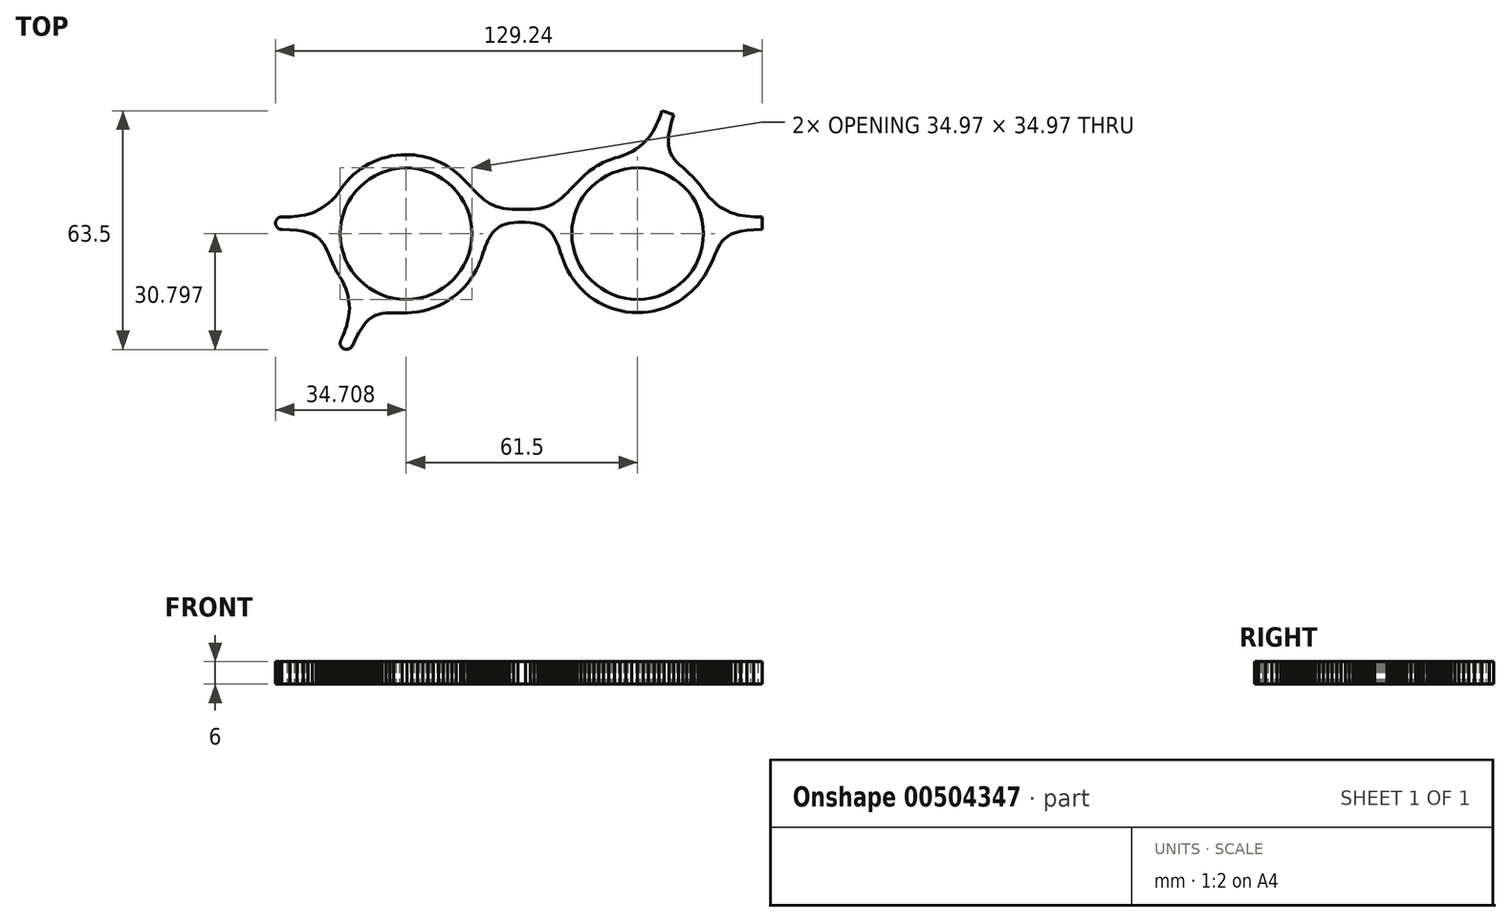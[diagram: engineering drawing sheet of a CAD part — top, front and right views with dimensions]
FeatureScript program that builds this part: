
annotation { "Feature Type Name" : "Feature", "Feature Type Description" : "" }
export const myFeature = defineFeature(function(context is Context, id is Id, definition is map)
    precondition{}
    {
        {
            var Q0;
            Q0=qCreatedBy(makeId("Top.planeOp"),FACE);
            var sketch = newSketch(context, id + "F0", { "sketchPlane" : qUnion([Q0])});
            skLineSegment(sketch, "E0", {"start": v(-47.15, 11.05) * mm, "end": v(-47.14, 11.06) * mm});
            skLineSegment(sketch, "E1", {"start": v(-47.14, 11.06) * mm, "end": v(-47.14, 11.06) * mm});
            skLineSegment(sketch, "E2", {"start": v(-47.14, 11.06) * mm, "end": v(-47.15, 11.05) * mm});
            skLineSegment(sketch, "E3", {"start": v(-47.15, 11.05) * mm, "end": v(-47.15, 11.05) * mm});
            skLineSegment(sketch, "E4", {"start": v(-47.15, 11.05) * mm, "end": v(-47.15, 11.04) * mm});
            skLineSegment(sketch, "E5", {"start": v(-47.15, 11.04) * mm, "end": v(-47.16, 11.04) * mm});
            skLineSegment(sketch, "E6", {"start": v(-47.16, 11.04) * mm, "end": v(-47.16, 11.04) * mm});
            skLineSegment(sketch, "E7", {"start": v(-47.16, 11.04) * mm, "end": v(-47.16, 11.03) * mm});
            skLineSegment(sketch, "E8", {"start": v(-47.16, 11.03) * mm, "end": v(-47.16, 11.03) * mm});
            skLineSegment(sketch, "E9", {"start": v(-47.16, 11.03) * mm, "end": v(-47.15, 11.04) * mm});
            skLineSegment(sketch, "E10", {"start": v(-47.15, 11.04) * mm, "end": v(-47.15, 11.05) * mm});
            skLineSegment(sketch, "E11", {"start": v(48.83, 11.04) * mm, "end": v(48.83, 11.04) * mm});
            skLineSegment(sketch, "E12", {"start": v(48.83, 11.04) * mm, "end": v(48.83, 11.05) * mm});
            skLineSegment(sketch, "E13", {"start": v(48.83, 11.05) * mm, "end": v(48.82, 11.05) * mm});
            skLineSegment(sketch, "E14", {"start": v(48.82, 11.05) * mm, "end": v(48.82, 11.05) * mm});
            skLineSegment(sketch, "E15", {"start": v(48.82, 11.05) * mm, "end": v(48.82, 11.06) * mm});
            skLineSegment(sketch, "E16", {"start": v(48.82, 11.06) * mm, "end": v(48.82, 11.06) * mm});
            skLineSegment(sketch, "E17", {"start": v(48.82, 11.06) * mm, "end": v(48.81, 11.06) * mm});
            skLineSegment(sketch, "E18", {"start": v(48.81, 11.06) * mm, "end": v(48.82, 11.06) * mm});
            skLineSegment(sketch, "E19", {"start": v(48.82, 11.06) * mm, "end": v(48.82, 11.05) * mm});
            skLineSegment(sketch, "E20", {"start": v(48.82, 11.05) * mm, "end": v(48.83, 11.04) * mm});
            skLineSegment(sketch, "E21", {"start": v(48.83, 11.04) * mm, "end": v(48.83, 11.03) * mm});
            skLineSegment(sketch, "E22", {"start": v(48.83, 11.03) * mm, "end": v(48.83, 11.03) * mm});
            skLineSegment(sketch, "E23", {"start": v(48.83, 11.03) * mm, "end": v(48.83, 11.04) * mm});
            skLineSegment(sketch, "E24", {"start": v(63.55, 3.53) * mm, "end": v(62.5, 3.56) * mm});
            skLineSegment(sketch, "E25", {"start": v(62.5, 3.56) * mm, "end": v(61.45, 3.62) * mm});
            skLineSegment(sketch, "E26", {"start": v(61.45, 3.62) * mm, "end": v(60.41, 3.72) * mm});
            skLineSegment(sketch, "E27", {"start": v(60.41, 3.72) * mm, "end": v(59.38, 3.86) * mm});
            skLineSegment(sketch, "E28", {"start": v(59.38, 3.86) * mm, "end": v(58.36, 4.07) * mm});
            skLineSegment(sketch, "E29", {"start": v(58.36, 4.07) * mm, "end": v(57.35, 4.33) * mm});
            skLineSegment(sketch, "E30", {"start": v(57.35, 4.33) * mm, "end": v(56.35, 4.67) * mm});
            skLineSegment(sketch, "E31", {"start": v(56.35, 4.67) * mm, "end": v(55.36, 5.1) * mm});
            skLineSegment(sketch, "E32", {"start": v(55.36, 5.1) * mm, "end": v(54.38, 5.6) * mm});
            skLineSegment(sketch, "E33", {"start": v(54.38, 5.6) * mm, "end": v(53.42, 6.21) * mm});
            skLineSegment(sketch, "E34", {"start": v(53.42, 6.21) * mm, "end": v(52.47, 6.93) * mm});
            skLineSegment(sketch, "E35", {"start": v(52.47, 6.93) * mm, "end": v(51.54, 7.76) * mm});
            skLineSegment(sketch, "E36", {"start": v(51.54, 7.76) * mm, "end": v(50.62, 8.72) * mm});
            skLineSegment(sketch, "E37", {"start": v(50.62, 8.72) * mm, "end": v(49.72, 9.8) * mm});
            skLineSegment(sketch, "E38", {"start": v(49.72, 9.8) * mm, "end": v(48.83, 11.03) * mm});
            skLineSegment(sketch, "E39", {"start": v(48.83, 11.03) * mm, "end": v(48.73, 11.17) * mm});
            skLineSegment(sketch, "E40", {"start": v(48.73, 11.17) * mm, "end": v(48.63, 11.31) * mm});
            skLineSegment(sketch, "E41", {"start": v(48.63, 11.31) * mm, "end": v(48.53, 11.45) * mm});
            skLineSegment(sketch, "E42", {"start": v(48.53, 11.45) * mm, "end": v(48.43, 11.59) * mm});
            skLineSegment(sketch, "E43", {"start": v(48.43, 11.59) * mm, "end": v(48.33, 11.72) * mm});
            skLineSegment(sketch, "E44", {"start": v(48.33, 11.72) * mm, "end": v(48.23, 11.86) * mm});
            skLineSegment(sketch, "E45", {"start": v(48.23, 11.86) * mm, "end": v(48.12, 12) * mm});
            skLineSegment(sketch, "E46", {"start": v(48.12, 12) * mm, "end": v(48.02, 12.13) * mm});
            skLineSegment(sketch, "E47", {"start": v(48.02, 12.13) * mm, "end": v(47.9, 12.26) * mm});
            skLineSegment(sketch, "E48", {"start": v(47.9, 12.26) * mm, "end": v(47.8, 12.4) * mm});
            skLineSegment(sketch, "E49", {"start": v(47.8, 12.4) * mm, "end": v(47.7, 12.52) * mm});
            skLineSegment(sketch, "E50", {"start": v(47.7, 12.52) * mm, "end": v(47.58, 12.65) * mm});
            skLineSegment(sketch, "E51", {"start": v(47.58, 12.65) * mm, "end": v(47.47, 12.78) * mm});
            skLineSegment(sketch, "E52", {"start": v(47.47, 12.78) * mm, "end": v(47.36, 12.91) * mm});
            skLineSegment(sketch, "E53", {"start": v(47.36, 12.91) * mm, "end": v(47.24, 13.04) * mm});
            skLineSegment(sketch, "E54", {"start": v(47.24, 13.04) * mm, "end": v(47.13, 13.16) * mm});
            skLineSegment(sketch, "E55", {"start": v(47.13, 13.16) * mm, "end": v(47.13, 13.16) * mm});
            skLineSegment(sketch, "E56", {"start": v(47.13, 13.16) * mm, "end": v(47.14, 13.16) * mm});
            skLineSegment(sketch, "E57", {"start": v(47.14, 13.16) * mm, "end": v(47.14, 13.16) * mm});
            skLineSegment(sketch, "E58", {"start": v(47.14, 13.16) * mm, "end": v(47.15, 13.16) * mm});
            skLineSegment(sketch, "E59", {"start": v(47.15, 13.16) * mm, "end": v(47.15, 13.16) * mm});
            skLineSegment(sketch, "E60", {"start": v(47.15, 13.16) * mm, "end": v(46.21, 14.17) * mm});
            skLineSegment(sketch, "E61", {"start": v(46.21, 14.17) * mm, "end": v(45.29, 15.08) * mm});
            skLineSegment(sketch, "E62", {"start": v(45.29, 15.08) * mm, "end": v(44.4, 15.9) * mm});
            skLineSegment(sketch, "E63", {"start": v(44.4, 15.9) * mm, "end": v(43.54, 16.66) * mm});
            skLineSegment(sketch, "E64", {"start": v(43.54, 16.66) * mm, "end": v(42.74, 17.39) * mm});
            skLineSegment(sketch, "E65", {"start": v(42.74, 17.39) * mm, "end": v(42, 18.11) * mm});
            skLineSegment(sketch, "E66", {"start": v(42, 18.11) * mm, "end": v(41.35, 18.85) * mm});
            skLineSegment(sketch, "E67", {"start": v(41.35, 18.85) * mm, "end": v(40.78, 19.64) * mm});
            skLineSegment(sketch, "E68", {"start": v(40.78, 19.64) * mm, "end": v(40.33, 20.5) * mm});
            skLineSegment(sketch, "E69", {"start": v(40.33, 20.5) * mm, "end": v(40, 21.44) * mm});
            skLineSegment(sketch, "E70", {"start": v(40, 21.44) * mm, "end": v(39.8, 22.52) * mm});
            skLineSegment(sketch, "E71", {"start": v(39.8, 22.52) * mm, "end": v(39.73, 23.75) * mm});
            skLineSegment(sketch, "E72", {"start": v(39.73, 23.75) * mm, "end": v(39.83, 25.15) * mm});
            skLineSegment(sketch, "E73", {"start": v(39.83, 25.15) * mm, "end": v(40.1, 26.75) * mm});
            skLineSegment(sketch, "E74", {"start": v(40.1, 26.75) * mm, "end": v(40.56, 28.58) * mm});
            skLineSegment(sketch, "E75", {"start": v(40.56, 28.58) * mm, "end": v(41.22, 30.66) * mm});
            skLineSegment(sketch, "E76", {"start": v(41.22, 30.66) * mm, "end": v(40.87, 30.78) * mm});
            skLineSegment(sketch, "E77", {"start": v(40.87, 30.78) * mm, "end": v(40.57, 30.88) * mm});
            skLineSegment(sketch, "E78", {"start": v(40.57, 30.88) * mm, "end": v(40.33, 30.96) * mm});
            skLineSegment(sketch, "E79", {"start": v(40.33, 30.96) * mm, "end": v(40.13, 31.03) * mm});
            skLineSegment(sketch, "E80", {"start": v(40.13, 31.03) * mm, "end": v(39.97, 31.09) * mm});
            skLineSegment(sketch, "E81", {"start": v(39.97, 31.09) * mm, "end": v(39.83, 31.13) * mm});
            skLineSegment(sketch, "E82", {"start": v(39.83, 31.13) * mm, "end": v(39.71, 31.17) * mm});
            skLineSegment(sketch, "E83", {"start": v(39.71, 31.17) * mm, "end": v(39.6, 31.21) * mm});
            skLineSegment(sketch, "E84", {"start": v(39.6, 31.21) * mm, "end": v(39.5, 31.25) * mm});
            skLineSegment(sketch, "E85", {"start": v(39.5, 31.25) * mm, "end": v(39.38, 31.29) * mm});
            skLineSegment(sketch, "E86", {"start": v(39.38, 31.29) * mm, "end": v(39.25, 31.33) * mm});
            skLineSegment(sketch, "E87", {"start": v(39.25, 31.33) * mm, "end": v(39.1, 31.39) * mm});
            skLineSegment(sketch, "E88", {"start": v(39.1, 31.39) * mm, "end": v(38.9, 31.45) * mm});
            skLineSegment(sketch, "E89", {"start": v(38.9, 31.45) * mm, "end": v(38.67, 31.53) * mm});
            skLineSegment(sketch, "E90", {"start": v(38.67, 31.53) * mm, "end": v(38.39, 31.63) * mm});
            skLineSegment(sketch, "E91", {"start": v(38.39, 31.63) * mm, "end": v(38.05, 31.75) * mm});
            skLineSegment(sketch, "E92", {"start": v(38.05, 31.75) * mm, "end": v(37.7, 30.77) * mm});
            skLineSegment(sketch, "E93", {"start": v(37.7, 30.77) * mm, "end": v(37.35, 29.8) * mm});
            skLineSegment(sketch, "E94", {"start": v(37.35, 29.8) * mm, "end": v(36.96, 28.86) * mm});
            skLineSegment(sketch, "E95", {"start": v(36.96, 28.86) * mm, "end": v(36.54, 27.93) * mm});
            skLineSegment(sketch, "E96", {"start": v(36.54, 27.93) * mm, "end": v(36.1, 27.02) * mm});
            skLineSegment(sketch, "E97", {"start": v(36.1, 27.02) * mm, "end": v(35.59, 26.14) * mm});
            skLineSegment(sketch, "E98", {"start": v(35.59, 26.14) * mm, "end": v(35.03, 25.29) * mm});
            skLineSegment(sketch, "E99", {"start": v(35.03, 25.29) * mm, "end": v(34.42, 24.47) * mm});
            skLineSegment(sketch, "E100", {"start": v(34.42, 24.47) * mm, "end": v(33.73, 23.68) * mm});
            skLineSegment(sketch, "E101", {"start": v(33.73, 23.68) * mm, "end": v(32.98, 22.93) * mm});
            skLineSegment(sketch, "E102", {"start": v(32.98, 22.93) * mm, "end": v(32.14, 22.23) * mm});
            skLineSegment(sketch, "E103", {"start": v(32.14, 22.23) * mm, "end": v(31.2, 21.57) * mm});
            skLineSegment(sketch, "E104", {"start": v(31.2, 21.57) * mm, "end": v(30.18, 20.95) * mm});
            skLineSegment(sketch, "E105", {"start": v(30.18, 20.95) * mm, "end": v(29.05, 20.39) * mm});
            skLineSegment(sketch, "E106", {"start": v(29.05, 20.39) * mm, "end": v(27.8, 19.88) * mm});
            skLineSegment(sketch, "E107", {"start": v(27.8, 19.88) * mm, "end": v(26.45, 19.42) * mm});
            skLineSegment(sketch, "E108", {"start": v(26.45, 19.42) * mm, "end": v(25.74, 19.23) * mm});
            skLineSegment(sketch, "E109", {"start": v(25.74, 19.23) * mm, "end": v(25.05, 19.02) * mm});
            skLineSegment(sketch, "E110", {"start": v(25.05, 19.02) * mm, "end": v(24.37, 18.78) * mm});
            skLineSegment(sketch, "E111", {"start": v(24.37, 18.78) * mm, "end": v(23.7, 18.52) * mm});
            skLineSegment(sketch, "E112", {"start": v(23.7, 18.52) * mm, "end": v(23.03, 18.24) * mm});
            skLineSegment(sketch, "E113", {"start": v(23.03, 18.24) * mm, "end": v(22.38, 17.93) * mm});
            skLineSegment(sketch, "E114", {"start": v(22.38, 17.93) * mm, "end": v(21.75, 17.6) * mm});
            skLineSegment(sketch, "E115", {"start": v(21.75, 17.6) * mm, "end": v(21.12, 17.26) * mm});
            skLineSegment(sketch, "E116", {"start": v(21.12, 17.26) * mm, "end": v(20.5, 16.9) * mm});
            skLineSegment(sketch, "E117", {"start": v(20.5, 16.9) * mm, "end": v(19.91, 16.5) * mm});
            skLineSegment(sketch, "E118", {"start": v(19.91, 16.5) * mm, "end": v(19.33, 16.1) * mm});
            skLineSegment(sketch, "E119", {"start": v(19.33, 16.1) * mm, "end": v(18.76, 15.68) * mm});
            skLineSegment(sketch, "E120", {"start": v(18.76, 15.68) * mm, "end": v(18.2, 15.23) * mm});
            skLineSegment(sketch, "E121", {"start": v(18.2, 15.23) * mm, "end": v(17.66, 14.77) * mm});
            skLineSegment(sketch, "E122", {"start": v(17.66, 14.77) * mm, "end": v(17.14, 14.3) * mm});
            skLineSegment(sketch, "E123", {"start": v(17.14, 14.3) * mm, "end": v(16.63, 13.8) * mm});
            skLineSegment(sketch, "E124", {"start": v(16.63, 13.8) * mm, "end": v(15.85, 13.01) * mm});
            skLineSegment(sketch, "E125", {"start": v(15.85, 13.01) * mm, "end": v(15.1, 12.24) * mm});
            skLineSegment(sketch, "E126", {"start": v(15.1, 12.24) * mm, "end": v(14.38, 11.48) * mm});
            skLineSegment(sketch, "E127", {"start": v(14.38, 11.48) * mm, "end": v(13.67, 10.75) * mm});
            skLineSegment(sketch, "E128", {"start": v(13.67, 10.75) * mm, "end": v(12.97, 10.03) * mm});
            skLineSegment(sketch, "E129", {"start": v(12.97, 10.03) * mm, "end": v(12.28, 9.36) * mm});
            skLineSegment(sketch, "E130", {"start": v(12.28, 9.36) * mm, "end": v(11.58, 8.71) * mm});
            skLineSegment(sketch, "E131", {"start": v(11.58, 8.71) * mm, "end": v(10.86, 8.12) * mm});
            skLineSegment(sketch, "E132", {"start": v(10.86, 8.12) * mm, "end": v(10.12, 7.57) * mm});
            skLineSegment(sketch, "E133", {"start": v(10.12, 7.57) * mm, "end": v(9.35, 7.08) * mm});
            skLineSegment(sketch, "E134", {"start": v(9.35, 7.08) * mm, "end": v(8.54, 6.64) * mm});
            skLineSegment(sketch, "E135", {"start": v(8.54, 6.64) * mm, "end": v(7.68, 6.27) * mm});
            skLineSegment(sketch, "E136", {"start": v(7.68, 6.27) * mm, "end": v(6.77, 5.98) * mm});
            skLineSegment(sketch, "E137", {"start": v(6.77, 5.98) * mm, "end": v(5.78, 5.76) * mm});
            skLineSegment(sketch, "E138", {"start": v(5.78, 5.76) * mm, "end": v(4.73, 5.63) * mm});
            skLineSegment(sketch, "E139", {"start": v(4.73, 5.63) * mm, "end": v(3.6, 5.58) * mm});
            skLineSegment(sketch, "E140", {"start": v(3.6, 5.58) * mm, "end": v(3.25, 5.58) * mm});
            skLineSegment(sketch, "E141", {"start": v(3.25, 5.58) * mm, "end": v(2.9, 5.58) * mm});
            skLineSegment(sketch, "E142", {"start": v(2.9, 5.58) * mm, "end": v(2.56, 5.58) * mm});
            skLineSegment(sketch, "E143", {"start": v(2.56, 5.58) * mm, "end": v(2.21, 5.58) * mm});
            skLineSegment(sketch, "E144", {"start": v(2.21, 5.58) * mm, "end": v(1.87, 5.58) * mm});
            skLineSegment(sketch, "E145", {"start": v(1.87, 5.58) * mm, "end": v(1.53, 5.58) * mm});
            skLineSegment(sketch, "E146", {"start": v(1.53, 5.58) * mm, "end": v(1.18, 5.58) * mm});
            skLineSegment(sketch, "E147", {"start": v(1.18, 5.58) * mm, "end": v(0.84, 5.58) * mm});
            skLineSegment(sketch, "E148", {"start": v(0.84, 5.58) * mm, "end": v(0.5, 5.58) * mm});
            skLineSegment(sketch, "E149", {"start": v(0.5, 5.58) * mm, "end": v(0.15, 5.58) * mm});
            skLineSegment(sketch, "E150", {"start": v(0.15, 5.58) * mm, "end": v(-0.2, 5.58) * mm});
            skLineSegment(sketch, "E151", {"start": v(-0.2, 5.58) * mm, "end": v(-0.54, 5.58) * mm});
            skLineSegment(sketch, "E152", {"start": v(-0.54, 5.58) * mm, "end": v(-0.88, 5.58) * mm});
            skLineSegment(sketch, "E153", {"start": v(-0.88, 5.58) * mm, "end": v(-1.23, 5.58) * mm});
            skLineSegment(sketch, "E154", {"start": v(-1.23, 5.58) * mm, "end": v(-1.57, 5.58) * mm});
            skLineSegment(sketch, "E155", {"start": v(-1.57, 5.58) * mm, "end": v(-1.92, 5.58) * mm});
            skLineSegment(sketch, "E156", {"start": v(-1.92, 5.58) * mm, "end": v(-3.05, 5.63) * mm});
            skLineSegment(sketch, "E157", {"start": v(-3.05, 5.63) * mm, "end": v(-4.1, 5.76) * mm});
            skLineSegment(sketch, "E158", {"start": v(-4.1, 5.76) * mm, "end": v(-5.1, 5.98) * mm});
            skLineSegment(sketch, "E159", {"start": v(-5.1, 5.98) * mm, "end": v(-6, 6.27) * mm});
            skLineSegment(sketch, "E160", {"start": v(-6, 6.27) * mm, "end": v(-6.87, 6.64) * mm});
            skLineSegment(sketch, "E161", {"start": v(-6.87, 6.64) * mm, "end": v(-7.68, 7.08) * mm});
            skLineSegment(sketch, "E162", {"start": v(-7.68, 7.08) * mm, "end": v(-8.45, 7.57) * mm});
            skLineSegment(sketch, "E163", {"start": v(-8.45, 7.57) * mm, "end": v(-9.19, 8.12) * mm});
            skLineSegment(sketch, "E164", {"start": v(-9.19, 8.12) * mm, "end": v(-9.9, 8.71) * mm});
            skLineSegment(sketch, "E165", {"start": v(-9.9, 8.71) * mm, "end": v(-10.6, 9.36) * mm});
            skLineSegment(sketch, "E166", {"start": v(-10.6, 9.36) * mm, "end": v(-11.3, 10.03) * mm});
            skLineSegment(sketch, "E167", {"start": v(-11.3, 10.03) * mm, "end": v(-12, 10.75) * mm});
            skLineSegment(sketch, "E168", {"start": v(-12, 10.75) * mm, "end": v(-12.7, 11.48) * mm});
            skLineSegment(sketch, "E169", {"start": v(-12.7, 11.48) * mm, "end": v(-13.42, 12.24) * mm});
            skLineSegment(sketch, "E170", {"start": v(-13.42, 12.24) * mm, "end": v(-14.17, 13.01) * mm});
            skLineSegment(sketch, "E171", {"start": v(-14.17, 13.01) * mm, "end": v(-14.96, 13.8) * mm});
            skLineSegment(sketch, "E172", {"start": v(-14.96, 13.8) * mm, "end": v(-15.7, 14.5) * mm});
            skLineSegment(sketch, "E173", {"start": v(-15.7, 14.5) * mm, "end": v(-16.46, 15.18) * mm});
            skLineSegment(sketch, "E174", {"start": v(-16.46, 15.18) * mm, "end": v(-17.25, 15.81) * mm});
            skLineSegment(sketch, "E175", {"start": v(-17.25, 15.81) * mm, "end": v(-18.08, 16.4) * mm});
            skLineSegment(sketch, "E176", {"start": v(-18.08, 16.4) * mm, "end": v(-18.94, 16.96) * mm});
            skLineSegment(sketch, "E177", {"start": v(-18.94, 16.96) * mm, "end": v(-19.83, 17.48) * mm});
            skLineSegment(sketch, "E178", {"start": v(-19.83, 17.48) * mm, "end": v(-20.74, 17.95) * mm});
            skLineSegment(sketch, "E179", {"start": v(-20.74, 17.95) * mm, "end": v(-21.67, 18.38) * mm});
            skLineSegment(sketch, "E180", {"start": v(-21.67, 18.38) * mm, "end": v(-22.64, 18.76) * mm});
            skLineSegment(sketch, "E181", {"start": v(-22.64, 18.76) * mm, "end": v(-23.62, 19.1) * mm});
            skLineSegment(sketch, "E182", {"start": v(-23.62, 19.1) * mm, "end": v(-24.62, 19.39) * mm});
            skLineSegment(sketch, "E183", {"start": v(-24.62, 19.39) * mm, "end": v(-25.65, 19.63) * mm});
            skLineSegment(sketch, "E184", {"start": v(-25.65, 19.63) * mm, "end": v(-26.69, 19.81) * mm});
            skLineSegment(sketch, "E185", {"start": v(-26.69, 19.81) * mm, "end": v(-27.75, 19.95) * mm});
            skLineSegment(sketch, "E186", {"start": v(-27.75, 19.95) * mm, "end": v(-28.82, 20.03) * mm});
            skLineSegment(sketch, "E187", {"start": v(-28.82, 20.03) * mm, "end": v(-29.91, 20.06) * mm});
            skLineSegment(sketch, "E188", {"start": v(-29.91, 20.06) * mm, "end": v(-31.24, 20.02) * mm});
            skLineSegment(sketch, "E189", {"start": v(-31.24, 20.02) * mm, "end": v(-32.55, 19.9) * mm});
            skLineSegment(sketch, "E190", {"start": v(-32.55, 19.9) * mm, "end": v(-33.83, 19.7) * mm});
            skLineSegment(sketch, "E191", {"start": v(-33.83, 19.7) * mm, "end": v(-35.08, 19.42) * mm});
            skLineSegment(sketch, "E192", {"start": v(-35.08, 19.42) * mm, "end": v(-36.3, 19.07) * mm});
            skLineSegment(sketch, "E193", {"start": v(-36.3, 19.07) * mm, "end": v(-37.5, 18.64) * mm});
            skLineSegment(sketch, "E194", {"start": v(-37.5, 18.64) * mm, "end": v(-38.66, 18.15) * mm});
            skLineSegment(sketch, "E195", {"start": v(-38.66, 18.15) * mm, "end": v(-39.78, 17.6) * mm});
            skLineSegment(sketch, "E196", {"start": v(-39.78, 17.6) * mm, "end": v(-40.87, 16.97) * mm});
            skLineSegment(sketch, "E197", {"start": v(-40.87, 16.97) * mm, "end": v(-41.91, 16.29) * mm});
            skLineSegment(sketch, "E198", {"start": v(-41.91, 16.29) * mm, "end": v(-42.91, 15.54) * mm});
            skLineSegment(sketch, "E199", {"start": v(-42.91, 15.54) * mm, "end": v(-43.86, 14.74) * mm});
            skLineSegment(sketch, "E200", {"start": v(-43.86, 14.74) * mm, "end": v(-44.77, 13.9) * mm});
            skLineSegment(sketch, "E201", {"start": v(-44.77, 13.9) * mm, "end": v(-45.62, 12.99) * mm});
            skLineSegment(sketch, "E202", {"start": v(-45.62, 12.99) * mm, "end": v(-46.42, 12.03) * mm});
            skLineSegment(sketch, "E203", {"start": v(-46.42, 12.03) * mm, "end": v(-47.16, 11.03) * mm});
            skLineSegment(sketch, "E204", {"start": v(-47.16, 11.03) * mm, "end": v(-47.97, 9.9) * mm});
            skLineSegment(sketch, "E205", {"start": v(-47.97, 9.9) * mm, "end": v(-48.8, 8.89) * mm});
            skLineSegment(sketch, "E206", {"start": v(-48.8, 8.89) * mm, "end": v(-49.64, 7.98) * mm});
            skLineSegment(sketch, "E207", {"start": v(-49.64, 7.98) * mm, "end": v(-50.5, 7.18) * mm});
            skLineSegment(sketch, "E208", {"start": v(-50.5, 7.18) * mm, "end": v(-51.36, 6.49) * mm});
            skLineSegment(sketch, "E209", {"start": v(-51.36, 6.49) * mm, "end": v(-52.24, 5.88) * mm});
            skLineSegment(sketch, "E210", {"start": v(-52.24, 5.88) * mm, "end": v(-53.13, 5.36) * mm});
            skLineSegment(sketch, "E211", {"start": v(-53.13, 5.36) * mm, "end": v(-54.03, 4.92) * mm});
            skLineSegment(sketch, "E212", {"start": v(-54.03, 4.92) * mm, "end": v(-54.95, 4.55) * mm});
            skLineSegment(sketch, "E213", {"start": v(-54.95, 4.55) * mm, "end": v(-55.87, 4.25) * mm});
            skLineSegment(sketch, "E214", {"start": v(-55.87, 4.25) * mm, "end": v(-56.8, 4.02) * mm});
            skLineSegment(sketch, "E215", {"start": v(-56.8, 4.02) * mm, "end": v(-57.73, 3.83) * mm});
            skLineSegment(sketch, "E216", {"start": v(-57.73, 3.83) * mm, "end": v(-58.68, 3.7) * mm});
            skLineSegment(sketch, "E217", {"start": v(-58.68, 3.7) * mm, "end": v(-59.63, 3.6) * mm});
            skLineSegment(sketch, "E218", {"start": v(-59.63, 3.6) * mm, "end": v(-60.58, 3.55) * mm});
            skLineSegment(sketch, "E219", {"start": v(-60.58, 3.55) * mm, "end": v(-61.54, 3.53) * mm});
            skLineSegment(sketch, "E220", {"start": v(-61.54, 3.53) * mm, "end": v(-61.63, 3.53) * mm});
            skLineSegment(sketch, "E221", {"start": v(-61.63, 3.53) * mm, "end": v(-61.72, 3.53) * mm});
            skLineSegment(sketch, "E222", {"start": v(-61.72, 3.53) * mm, "end": v(-61.8, 3.52) * mm});
            skLineSegment(sketch, "E223", {"start": v(-61.8, 3.52) * mm, "end": v(-61.9, 3.52) * mm});
            skLineSegment(sketch, "E224", {"start": v(-61.9, 3.52) * mm, "end": v(-61.98, 3.52) * mm});
            skLineSegment(sketch, "E225", {"start": v(-61.98, 3.52) * mm, "end": v(-62.07, 3.52) * mm});
            skLineSegment(sketch, "E226", {"start": v(-62.07, 3.52) * mm, "end": v(-62.16, 3.52) * mm});
            skLineSegment(sketch, "E227", {"start": v(-62.16, 3.52) * mm, "end": v(-62.24, 3.52) * mm});
            skLineSegment(sketch, "E228", {"start": v(-62.24, 3.52) * mm, "end": v(-62.33, 3.52) * mm});
            skLineSegment(sketch, "E229", {"start": v(-62.33, 3.52) * mm, "end": v(-62.42, 3.52) * mm});
            skLineSegment(sketch, "E230", {"start": v(-62.42, 3.52) * mm, "end": v(-62.5, 3.52) * mm});
            skLineSegment(sketch, "E231", {"start": v(-62.5, 3.52) * mm, "end": v(-62.6, 3.52) * mm});
            skLineSegment(sketch, "E232", {"start": v(-62.6, 3.52) * mm, "end": v(-62.68, 3.52) * mm});
            skLineSegment(sketch, "E233", {"start": v(-62.68, 3.52) * mm, "end": v(-62.77, 3.52) * mm});
            skLineSegment(sketch, "E234", {"start": v(-62.77, 3.52) * mm, "end": v(-62.85, 3.52) * mm});
            skLineSegment(sketch, "E235", {"start": v(-62.85, 3.52) * mm, "end": v(-62.94, 3.52) * mm});
            skLineSegment(sketch, "E236", {"start": v(-62.94, 3.52) * mm, "end": v(-62.94, 3.52) * mm});
            skLineSegment(sketch, "E237", {"start": v(-62.94, 3.52) * mm, "end": v(-63.11, 3.5) * mm});
            skLineSegment(sketch, "E238", {"start": v(-63.11, 3.5) * mm, "end": v(-63.28, 3.48) * mm});
            skLineSegment(sketch, "E239", {"start": v(-63.28, 3.48) * mm, "end": v(-63.44, 3.44) * mm});
            skLineSegment(sketch, "E240", {"start": v(-63.44, 3.44) * mm, "end": v(-63.6, 3.39) * mm});
            skLineSegment(sketch, "E241", {"start": v(-63.6, 3.39) * mm, "end": v(-63.74, 3.31) * mm});
            skLineSegment(sketch, "E242", {"start": v(-63.74, 3.31) * mm, "end": v(-63.88, 3.23) * mm});
            skLineSegment(sketch, "E243", {"start": v(-63.88, 3.23) * mm, "end": v(-64, 3.13) * mm});
            skLineSegment(sketch, "E244", {"start": v(-64, 3.13) * mm, "end": v(-64.12, 3.03) * mm});
            skLineSegment(sketch, "E245", {"start": v(-64.12, 3.03) * mm, "end": v(-64.23, 2.9) * mm});
            skLineSegment(sketch, "E246", {"start": v(-64.23, 2.9) * mm, "end": v(-64.33, 2.78) * mm});
            skLineSegment(sketch, "E247", {"start": v(-64.33, 2.78) * mm, "end": v(-64.41, 2.64) * mm});
            skLineSegment(sketch, "E248", {"start": v(-64.41, 2.64) * mm, "end": v(-64.48, 2.5) * mm});
            skLineSegment(sketch, "E249", {"start": v(-64.48, 2.5) * mm, "end": v(-64.54, 2.34) * mm});
            skLineSegment(sketch, "E250", {"start": v(-64.54, 2.34) * mm, "end": v(-64.58, 2.18) * mm});
            skLineSegment(sketch, "E251", {"start": v(-64.58, 2.18) * mm, "end": v(-64.6, 2.01) * mm});
            skLineSegment(sketch, "E252", {"start": v(-64.6, 2.01) * mm, "end": v(-64.62, 1.84) * mm});
            skLineSegment(sketch, "E253", {"start": v(-64.62, 1.84) * mm, "end": v(-64.6, 1.67) * mm});
            skLineSegment(sketch, "E254", {"start": v(-64.6, 1.67) * mm, "end": v(-64.58, 1.5) * mm});
            skLineSegment(sketch, "E255", {"start": v(-64.58, 1.5) * mm, "end": v(-64.54, 1.34) * mm});
            skLineSegment(sketch, "E256", {"start": v(-64.54, 1.34) * mm, "end": v(-64.48, 1.19) * mm});
            skLineSegment(sketch, "E257", {"start": v(-64.48, 1.19) * mm, "end": v(-64.41, 1.04) * mm});
            skLineSegment(sketch, "E258", {"start": v(-64.41, 1.04) * mm, "end": v(-64.33, 0.9) * mm});
            skLineSegment(sketch, "E259", {"start": v(-64.33, 0.9) * mm, "end": v(-64.23, 0.78) * mm});
            skLineSegment(sketch, "E260", {"start": v(-64.23, 0.78) * mm, "end": v(-64.12, 0.66) * mm});
            skLineSegment(sketch, "E261", {"start": v(-64.12, 0.66) * mm, "end": v(-64, 0.55) * mm});
            skLineSegment(sketch, "E262", {"start": v(-64, 0.55) * mm, "end": v(-63.88, 0.45) * mm});
            skLineSegment(sketch, "E263", {"start": v(-63.88, 0.45) * mm, "end": v(-63.74, 0.37) * mm});
            skLineSegment(sketch, "E264", {"start": v(-63.74, 0.37) * mm, "end": v(-63.6, 0.3) * mm});
            skLineSegment(sketch, "E265", {"start": v(-63.6, 0.3) * mm, "end": v(-63.44, 0.24) * mm});
            skLineSegment(sketch, "E266", {"start": v(-63.44, 0.24) * mm, "end": v(-63.28, 0.2) * mm});
            skLineSegment(sketch, "E267", {"start": v(-63.28, 0.2) * mm, "end": v(-63.11, 0.18) * mm});
            skLineSegment(sketch, "E268", {"start": v(-63.11, 0.18) * mm, "end": v(-62.94, 0.17) * mm});
            skLineSegment(sketch, "E269", {"start": v(-62.94, 0.17) * mm, "end": v(-62.94, 0.17) * mm});
            skLineSegment(sketch, "E270", {"start": v(-62.94, 0.17) * mm, "end": v(-60.76, 0.11) * mm});
            skLineSegment(sketch, "E271", {"start": v(-60.76, 0.11) * mm, "end": v(-58.88, -0.05) * mm});
            skLineSegment(sketch, "E272", {"start": v(-58.88, -0.05) * mm, "end": v(-57.28, -0.3) * mm});
            skLineSegment(sketch, "E273", {"start": v(-57.28, -0.3) * mm, "end": v(-55.92, -0.66) * mm});
            skLineSegment(sketch, "E274", {"start": v(-55.92, -0.66) * mm, "end": v(-54.78, -1.12) * mm});
            skLineSegment(sketch, "E275", {"start": v(-54.78, -1.12) * mm, "end": v(-53.82, -1.66) * mm});
            skLineSegment(sketch, "E276", {"start": v(-53.82, -1.66) * mm, "end": v(-53.03, -2.28) * mm});
            skLineSegment(sketch, "E277", {"start": v(-53.03, -2.28) * mm, "end": v(-52.37, -2.99) * mm});
            skLineSegment(sketch, "E278", {"start": v(-52.37, -2.99) * mm, "end": v(-51.8, -3.77) * mm});
            skLineSegment(sketch, "E279", {"start": v(-51.8, -3.77) * mm, "end": v(-51.32, -4.63) * mm});
            skLineSegment(sketch, "E280", {"start": v(-51.32, -4.63) * mm, "end": v(-50.88, -5.56) * mm});
            skLineSegment(sketch, "E281", {"start": v(-50.88, -5.56) * mm, "end": v(-50.45, -6.55) * mm});
            skLineSegment(sketch, "E282", {"start": v(-50.45, -6.55) * mm, "end": v(-50, -7.6) * mm});
            skLineSegment(sketch, "E283", {"start": v(-50, -7.6) * mm, "end": v(-49.52, -8.72) * mm});
            skLineSegment(sketch, "E284", {"start": v(-49.52, -8.72) * mm, "end": v(-48.96, -9.89) * mm});
            skLineSegment(sketch, "E285", {"start": v(-48.96, -9.89) * mm, "end": v(-48.3, -11.1) * mm});
            skLineSegment(sketch, "E286", {"start": v(-48.3, -11.1) * mm, "end": v(-48.27, -11.17) * mm});
            skLineSegment(sketch, "E287", {"start": v(-48.27, -11.17) * mm, "end": v(-48.23, -11.24) * mm});
            skLineSegment(sketch, "E288", {"start": v(-48.23, -11.24) * mm, "end": v(-48.2, -11.3) * mm});
            skLineSegment(sketch, "E289", {"start": v(-48.2, -11.3) * mm, "end": v(-48.16, -11.37) * mm});
            skLineSegment(sketch, "E290", {"start": v(-48.16, -11.37) * mm, "end": v(-48.12, -11.43) * mm});
            skLineSegment(sketch, "E291", {"start": v(-48.12, -11.43) * mm, "end": v(-48.08, -11.5) * mm});
            skLineSegment(sketch, "E292", {"start": v(-48.08, -11.5) * mm, "end": v(-48.04, -11.56) * mm});
            skLineSegment(sketch, "E293", {"start": v(-48.04, -11.56) * mm, "end": v(-48, -11.62) * mm});
            skLineSegment(sketch, "E294", {"start": v(-48, -11.62) * mm, "end": v(-47.97, -11.69) * mm});
            skLineSegment(sketch, "E295", {"start": v(-47.97, -11.69) * mm, "end": v(-47.93, -11.75) * mm});
            skLineSegment(sketch, "E296", {"start": v(-47.93, -11.75) * mm, "end": v(-47.9, -11.81) * mm});
            skLineSegment(sketch, "E297", {"start": v(-47.9, -11.81) * mm, "end": v(-47.85, -11.88) * mm});
            skLineSegment(sketch, "E298", {"start": v(-47.85, -11.88) * mm, "end": v(-47.81, -11.94) * mm});
            skLineSegment(sketch, "E299", {"start": v(-47.81, -11.94) * mm, "end": v(-47.77, -12) * mm});
            skLineSegment(sketch, "E300", {"start": v(-47.77, -12) * mm, "end": v(-47.73, -12.06) * mm});
            skLineSegment(sketch, "E301", {"start": v(-47.73, -12.06) * mm, "end": v(-47.7, -12.13) * mm});
            skLineSegment(sketch, "E302", {"start": v(-47.7, -12.13) * mm, "end": v(-47.01, -13.3) * mm});
            skLineSegment(sketch, "E303", {"start": v(-47.01, -13.3) * mm, "end": v(-46.44, -14.46) * mm});
            skLineSegment(sketch, "E304", {"start": v(-46.44, -14.46) * mm, "end": v(-45.97, -15.57) * mm});
            skLineSegment(sketch, "E305", {"start": v(-45.97, -15.57) * mm, "end": v(-45.6, -16.66) * mm});
            skLineSegment(sketch, "E306", {"start": v(-45.6, -16.66) * mm, "end": v(-45.32, -17.72) * mm});
            skLineSegment(sketch, "E307", {"start": v(-45.32, -17.72) * mm, "end": v(-45.13, -18.76) * mm});
            skLineSegment(sketch, "E308", {"start": v(-45.13, -18.76) * mm, "end": v(-45.02, -19.77) * mm});
            skLineSegment(sketch, "E309", {"start": v(-45.02, -19.77) * mm, "end": v(-44.99, -20.76) * mm});
            skLineSegment(sketch, "E310", {"start": v(-44.99, -20.76) * mm, "end": v(-45.02, -21.73) * mm});
            skLineSegment(sketch, "E311", {"start": v(-45.02, -21.73) * mm, "end": v(-45.12, -22.68) * mm});
            skLineSegment(sketch, "E312", {"start": v(-45.12, -22.68) * mm, "end": v(-45.28, -23.62) * mm});
            skLineSegment(sketch, "E313", {"start": v(-45.28, -23.62) * mm, "end": v(-45.5, -24.54) * mm});
            skLineSegment(sketch, "E314", {"start": v(-45.5, -24.54) * mm, "end": v(-45.75, -25.45) * mm});
            skLineSegment(sketch, "E315", {"start": v(-45.75, -25.45) * mm, "end": v(-46.04, -26.34) * mm});
            skLineSegment(sketch, "E316", {"start": v(-46.04, -26.34) * mm, "end": v(-46.37, -27.23) * mm});
            skLineSegment(sketch, "E317", {"start": v(-46.37, -27.23) * mm, "end": v(-46.73, -28.11) * mm});
            skLineSegment(sketch, "E318", {"start": v(-46.73, -28.11) * mm, "end": v(-46.76, -28.2) * mm});
            skLineSegment(sketch, "E319", {"start": v(-46.76, -28.2) * mm, "end": v(-46.8, -28.27) * mm});
            skLineSegment(sketch, "E320", {"start": v(-46.8, -28.27) * mm, "end": v(-46.83, -28.35) * mm});
            skLineSegment(sketch, "E321", {"start": v(-46.83, -28.35) * mm, "end": v(-46.87, -28.43) * mm});
            skLineSegment(sketch, "E322", {"start": v(-46.87, -28.43) * mm, "end": v(-46.9, -28.51) * mm});
            skLineSegment(sketch, "E323", {"start": v(-46.9, -28.51) * mm, "end": v(-46.94, -28.6) * mm});
            skLineSegment(sketch, "E324", {"start": v(-46.94, -28.6) * mm, "end": v(-46.97, -28.68) * mm});
            skLineSegment(sketch, "E325", {"start": v(-46.97, -28.68) * mm, "end": v(-47, -28.76) * mm});
            skLineSegment(sketch, "E326", {"start": v(-47, -28.76) * mm, "end": v(-47.04, -28.83) * mm});
            skLineSegment(sketch, "E327", {"start": v(-47.04, -28.83) * mm, "end": v(-47.08, -28.92) * mm});
            skLineSegment(sketch, "E328", {"start": v(-47.08, -28.92) * mm, "end": v(-47.11, -29) * mm});
            skLineSegment(sketch, "E329", {"start": v(-47.11, -29) * mm, "end": v(-47.15, -29.08) * mm});
            skLineSegment(sketch, "E330", {"start": v(-47.15, -29.08) * mm, "end": v(-47.18, -29.16) * mm});
            skLineSegment(sketch, "E331", {"start": v(-47.18, -29.16) * mm, "end": v(-47.21, -29.24) * mm});
            skLineSegment(sketch, "E332", {"start": v(-47.21, -29.24) * mm, "end": v(-47.25, -29.32) * mm});
            skLineSegment(sketch, "E333", {"start": v(-47.25, -29.32) * mm, "end": v(-47.28, -29.4) * mm});
            skLineSegment(sketch, "E334", {"start": v(-47.28, -29.4) * mm, "end": v(-47.28, -29.4) * mm});
            skLineSegment(sketch, "E335", {"start": v(-47.28, -29.4) * mm, "end": v(-47.34, -29.56) * mm});
            skLineSegment(sketch, "E336", {"start": v(-47.34, -29.56) * mm, "end": v(-47.39, -29.72) * mm});
            skLineSegment(sketch, "E337", {"start": v(-47.39, -29.72) * mm, "end": v(-47.41, -29.88) * mm});
            skLineSegment(sketch, "E338", {"start": v(-47.41, -29.88) * mm, "end": v(-47.42, -30.05) * mm});
            skLineSegment(sketch, "E339", {"start": v(-47.42, -30.05) * mm, "end": v(-47.42, -30.2) * mm});
            skLineSegment(sketch, "E340", {"start": v(-47.42, -30.2) * mm, "end": v(-47.4, -30.37) * mm});
            skLineSegment(sketch, "E341", {"start": v(-47.4, -30.37) * mm, "end": v(-47.36, -30.53) * mm});
            skLineSegment(sketch, "E342", {"start": v(-47.36, -30.53) * mm, "end": v(-47.3, -30.68) * mm});
            skLineSegment(sketch, "E343", {"start": v(-47.3, -30.68) * mm, "end": v(-47.24, -30.82) * mm});
            skLineSegment(sketch, "E344", {"start": v(-47.24, -30.82) * mm, "end": v(-47.17, -30.97) * mm});
            skLineSegment(sketch, "E345", {"start": v(-47.17, -30.97) * mm, "end": v(-47.07, -31.1) * mm});
            skLineSegment(sketch, "E346", {"start": v(-47.07, -31.1) * mm, "end": v(-46.97, -31.22) * mm});
            skLineSegment(sketch, "E347", {"start": v(-46.97, -31.22) * mm, "end": v(-46.85, -31.33) * mm});
            skLineSegment(sketch, "E348", {"start": v(-46.85, -31.33) * mm, "end": v(-46.72, -31.44) * mm});
            skLineSegment(sketch, "E349", {"start": v(-46.72, -31.44) * mm, "end": v(-46.58, -31.53) * mm});
            skLineSegment(sketch, "E350", {"start": v(-46.58, -31.53) * mm, "end": v(-46.42, -31.6) * mm});
            skLineSegment(sketch, "E351", {"start": v(-46.42, -31.6) * mm, "end": v(-46.26, -31.66) * mm});
            skLineSegment(sketch, "E352", {"start": v(-46.26, -31.66) * mm, "end": v(-46.1, -31.7) * mm});
            skLineSegment(sketch, "E353", {"start": v(-46.1, -31.7) * mm, "end": v(-45.94, -31.74) * mm});
            skLineSegment(sketch, "E354", {"start": v(-45.94, -31.74) * mm, "end": v(-45.77, -31.75) * mm});
            skLineSegment(sketch, "E355", {"start": v(-45.77, -31.75) * mm, "end": v(-45.61, -31.74) * mm});
            skLineSegment(sketch, "E356", {"start": v(-45.61, -31.74) * mm, "end": v(-45.45, -31.72) * mm});
            skLineSegment(sketch, "E357", {"start": v(-45.45, -31.72) * mm, "end": v(-45.3, -31.68) * mm});
            skLineSegment(sketch, "E358", {"start": v(-45.3, -31.68) * mm, "end": v(-45.14, -31.63) * mm});
            skLineSegment(sketch, "E359", {"start": v(-45.14, -31.63) * mm, "end": v(-45, -31.56) * mm});
            skLineSegment(sketch, "E360", {"start": v(-45, -31.56) * mm, "end": v(-44.85, -31.49) * mm});
            skLineSegment(sketch, "E361", {"start": v(-44.85, -31.49) * mm, "end": v(-44.72, -31.4) * mm});
            skLineSegment(sketch, "E362", {"start": v(-44.72, -31.4) * mm, "end": v(-44.6, -31.29) * mm});
            skLineSegment(sketch, "E363", {"start": v(-44.6, -31.29) * mm, "end": v(-44.48, -31.17) * mm});
            skLineSegment(sketch, "E364", {"start": v(-44.48, -31.17) * mm, "end": v(-44.38, -31.04) * mm});
            skLineSegment(sketch, "E365", {"start": v(-44.38, -31.04) * mm, "end": v(-44.3, -30.9) * mm});
            skLineSegment(sketch, "E366", {"start": v(-44.3, -30.9) * mm, "end": v(-44.22, -30.74) * mm});
            skLineSegment(sketch, "E367", {"start": v(-44.22, -30.74) * mm, "end": v(-44.22, -30.74) * mm});
            skLineSegment(sketch, "E368", {"start": v(-44.22, -30.74) * mm, "end": v(-44.21, -30.74) * mm});
            skLineSegment(sketch, "E369", {"start": v(-44.21, -30.74) * mm, "end": v(-44.21, -30.74) * mm});
            skLineSegment(sketch, "E370", {"start": v(-44.21, -30.74) * mm, "end": v(-43.3, -28.8) * mm});
            skLineSegment(sketch, "E371", {"start": v(-43.3, -28.8) * mm, "end": v(-42.41, -27.16) * mm});
            skLineSegment(sketch, "E372", {"start": v(-42.41, -27.16) * mm, "end": v(-41.54, -25.8) * mm});
            skLineSegment(sketch, "E373", {"start": v(-41.54, -25.8) * mm, "end": v(-40.69, -24.7) * mm});
            skLineSegment(sketch, "E374", {"start": v(-40.69, -24.7) * mm, "end": v(-39.83, -23.84) * mm});
            skLineSegment(sketch, "E375", {"start": v(-39.83, -23.84) * mm, "end": v(-38.96, -23.18) * mm});
            skLineSegment(sketch, "E376", {"start": v(-38.96, -23.18) * mm, "end": v(-38.09, -22.7) * mm});
            skLineSegment(sketch, "E377", {"start": v(-38.09, -22.7) * mm, "end": v(-37.2, -22.37) * mm});
            skLineSegment(sketch, "E378", {"start": v(-37.2, -22.37) * mm, "end": v(-36.27, -22.16) * mm});
            skLineSegment(sketch, "E379", {"start": v(-36.27, -22.16) * mm, "end": v(-35.3, -22.04) * mm});
            skLineSegment(sketch, "E380", {"start": v(-35.3, -22.04) * mm, "end": v(-34.3, -22) * mm});
            skLineSegment(sketch, "E381", {"start": v(-34.3, -22) * mm, "end": v(-33.25, -22) * mm});
            skLineSegment(sketch, "E382", {"start": v(-33.25, -22) * mm, "end": v(-32.13, -22.02) * mm});
            skLineSegment(sketch, "E383", {"start": v(-32.13, -22.02) * mm, "end": v(-30.95, -22.03) * mm});
            skLineSegment(sketch, "E384", {"start": v(-30.95, -22.03) * mm, "end": v(-29.7, -22) * mm});
            skLineSegment(sketch, "E385", {"start": v(-29.7, -22) * mm, "end": v(-28.36, -21.9) * mm});
            skLineSegment(sketch, "E386", {"start": v(-28.36, -21.9) * mm, "end": v(-26.89, -21.75) * mm});
            skLineSegment(sketch, "E387", {"start": v(-26.89, -21.75) * mm, "end": v(-25.45, -21.49) * mm});
            skLineSegment(sketch, "E388", {"start": v(-25.45, -21.49) * mm, "end": v(-24.05, -21.13) * mm});
            skLineSegment(sketch, "E389", {"start": v(-24.05, -21.13) * mm, "end": v(-22.68, -20.68) * mm});
            skLineSegment(sketch, "E390", {"start": v(-22.68, -20.68) * mm, "end": v(-21.36, -20.14) * mm});
            skLineSegment(sketch, "E391", {"start": v(-21.36, -20.14) * mm, "end": v(-20.08, -19.52) * mm});
            skLineSegment(sketch, "E392", {"start": v(-20.08, -19.52) * mm, "end": v(-18.85, -18.81) * mm});
            skLineSegment(sketch, "E393", {"start": v(-18.85, -18.81) * mm, "end": v(-17.68, -18.03) * mm});
            skLineSegment(sketch, "E394", {"start": v(-17.68, -18.03) * mm, "end": v(-16.57, -17.17) * mm});
            skLineSegment(sketch, "E395", {"start": v(-16.57, -17.17) * mm, "end": v(-15.51, -16.24) * mm});
            skLineSegment(sketch, "E396", {"start": v(-15.51, -16.24) * mm, "end": v(-14.52, -15.24) * mm});
            skLineSegment(sketch, "E397", {"start": v(-14.52, -15.24) * mm, "end": v(-13.6, -14.18) * mm});
            skLineSegment(sketch, "E398", {"start": v(-13.6, -14.18) * mm, "end": v(-12.75, -13.06) * mm});
            skLineSegment(sketch, "E399", {"start": v(-12.75, -13.06) * mm, "end": v(-11.97, -11.88) * mm});
            skLineSegment(sketch, "E400", {"start": v(-11.97, -11.88) * mm, "end": v(-11.28, -10.64) * mm});
            skLineSegment(sketch, "E401", {"start": v(-11.28, -10.64) * mm, "end": v(-10.66, -9.36) * mm});
            skLineSegment(sketch, "E402", {"start": v(-10.66, -9.36) * mm, "end": v(-10.65, -9.34) * mm});
            skLineSegment(sketch, "E403", {"start": v(-10.65, -9.34) * mm, "end": v(-10.63, -9.3) * mm});
            skLineSegment(sketch, "E404", {"start": v(-10.63, -9.3) * mm, "end": v(-10.6, -9.2) * mm});
            skLineSegment(sketch, "E405", {"start": v(-10.6, -9.2) * mm, "end": v(-10.55, -9.1) * mm});
            skLineSegment(sketch, "E406", {"start": v(-10.55, -9.1) * mm, "end": v(-10.5, -8.96) * mm});
            skLineSegment(sketch, "E407", {"start": v(-10.5, -8.96) * mm, "end": v(-10.44, -8.8) * mm});
            skLineSegment(sketch, "E408", {"start": v(-10.44, -8.8) * mm, "end": v(-10.37, -8.63) * mm});
            skLineSegment(sketch, "E409", {"start": v(-10.37, -8.63) * mm, "end": v(-10.3, -8.44) * mm});
            skLineSegment(sketch, "E410", {"start": v(-10.3, -8.44) * mm, "end": v(-10.23, -8.25) * mm});
            skLineSegment(sketch, "E411", {"start": v(-10.23, -8.25) * mm, "end": v(-10.15, -8.05) * mm});
            skLineSegment(sketch, "E412", {"start": v(-10.15, -8.05) * mm, "end": v(-10.08, -7.84) * mm});
            skLineSegment(sketch, "E413", {"start": v(-10.08, -7.84) * mm, "end": v(-10, -7.64) * mm});
            skLineSegment(sketch, "E414", {"start": v(-10, -7.64) * mm, "end": v(-9.94, -7.44) * mm});
            skLineSegment(sketch, "E415", {"start": v(-9.94, -7.44) * mm, "end": v(-9.87, -7.25) * mm});
            skLineSegment(sketch, "E416", {"start": v(-9.87, -7.25) * mm, "end": v(-9.81, -7.07) * mm});
            skLineSegment(sketch, "E417", {"start": v(-9.81, -7.07) * mm, "end": v(-9.76, -6.9) * mm});
            skLineSegment(sketch, "E418", {"start": v(-9.76, -6.9) * mm, "end": v(-9.45, -6) * mm});
            skLineSegment(sketch, "E419", {"start": v(-9.45, -6) * mm, "end": v(-9.15, -5.13) * mm});
            skLineSegment(sketch, "E420", {"start": v(-9.15, -5.13) * mm, "end": v(-8.84, -4.28) * mm});
            skLineSegment(sketch, "E421", {"start": v(-8.84, -4.28) * mm, "end": v(-8.51, -3.46) * mm});
            skLineSegment(sketch, "E422", {"start": v(-8.51, -3.46) * mm, "end": v(-8.16, -2.68) * mm});
            skLineSegment(sketch, "E423", {"start": v(-8.16, -2.68) * mm, "end": v(-7.77, -1.94) * mm});
            skLineSegment(sketch, "E424", {"start": v(-7.77, -1.94) * mm, "end": v(-7.35, -1.25) * mm});
            skLineSegment(sketch, "E425", {"start": v(-7.35, -1.25) * mm, "end": v(-6.87, -0.61) * mm});
            skLineSegment(sketch, "E426", {"start": v(-6.87, -0.61) * mm, "end": v(-6.33, -0.03) * mm});
            skLineSegment(sketch, "E427", {"start": v(-6.33, -0.03) * mm, "end": v(-5.73, 0.5) * mm});
            skLineSegment(sketch, "E428", {"start": v(-5.73, 0.5) * mm, "end": v(-5.04, 0.95) * mm});
            skLineSegment(sketch, "E429", {"start": v(-5.04, 0.95) * mm, "end": v(-4.28, 1.33) * mm});
            skLineSegment(sketch, "E430", {"start": v(-4.28, 1.33) * mm, "end": v(-3.41, 1.64) * mm});
            skLineSegment(sketch, "E431", {"start": v(-3.41, 1.64) * mm, "end": v(-2.44, 1.87) * mm});
            skLineSegment(sketch, "E432", {"start": v(-2.44, 1.87) * mm, "end": v(-1.36, 2) * mm});
            skLineSegment(sketch, "E433", {"start": v(-1.36, 2) * mm, "end": v(-0.16, 2.05) * mm});
            skLineSegment(sketch, "E434", {"start": v(-0.16, 2.05) * mm, "end": v(-0.04, 2.05) * mm});
            skLineSegment(sketch, "E435", {"start": v(-0.04, 2.05) * mm, "end": v(0.09, 2.05) * mm});
            skLineSegment(sketch, "E436", {"start": v(0.09, 2.05) * mm, "end": v(0.21, 2.05) * mm});
            skLineSegment(sketch, "E437", {"start": v(0.21, 2.05) * mm, "end": v(0.34, 2.05) * mm});
            skLineSegment(sketch, "E438", {"start": v(0.34, 2.05) * mm, "end": v(0.46, 2.05) * mm});
            skLineSegment(sketch, "E439", {"start": v(0.46, 2.05) * mm, "end": v(0.59, 2.05) * mm});
            skLineSegment(sketch, "E440", {"start": v(0.59, 2.05) * mm, "end": v(0.71, 2.05) * mm});
            skLineSegment(sketch, "E441", {"start": v(0.71, 2.05) * mm, "end": v(0.84, 2.05) * mm});
            skLineSegment(sketch, "E442", {"start": v(0.84, 2.05) * mm, "end": v(0.96, 2.05) * mm});
            skLineSegment(sketch, "E443", {"start": v(0.96, 2.05) * mm, "end": v(1.09, 2.05) * mm});
            skLineSegment(sketch, "E444", {"start": v(1.09, 2.05) * mm, "end": v(1.21, 2.05) * mm});
            skLineSegment(sketch, "E445", {"start": v(1.21, 2.05) * mm, "end": v(1.34, 2.05) * mm});
            skLineSegment(sketch, "E446", {"start": v(1.34, 2.05) * mm, "end": v(1.46, 2.05) * mm});
            skLineSegment(sketch, "E447", {"start": v(1.46, 2.05) * mm, "end": v(1.59, 2.05) * mm});
            skLineSegment(sketch, "E448", {"start": v(1.59, 2.05) * mm, "end": v(1.71, 2.05) * mm});
            skLineSegment(sketch, "E449", {"start": v(1.71, 2.05) * mm, "end": v(1.84, 2.05) * mm});
            skLineSegment(sketch, "E450", {"start": v(1.84, 2.05) * mm, "end": v(3.04, 2) * mm});
            skLineSegment(sketch, "E451", {"start": v(3.04, 2) * mm, "end": v(4.12, 1.87) * mm});
            skLineSegment(sketch, "E452", {"start": v(4.12, 1.87) * mm, "end": v(5.09, 1.64) * mm});
            skLineSegment(sketch, "E453", {"start": v(5.09, 1.64) * mm, "end": v(5.95, 1.33) * mm});
            skLineSegment(sketch, "E454", {"start": v(5.95, 1.33) * mm, "end": v(6.72, 0.95) * mm});
            skLineSegment(sketch, "E455", {"start": v(6.72, 0.95) * mm, "end": v(7.4, 0.5) * mm});
            skLineSegment(sketch, "E456", {"start": v(7.4, 0.5) * mm, "end": v(8, -0.03) * mm});
            skLineSegment(sketch, "E457", {"start": v(8, -0.03) * mm, "end": v(8.55, -0.61) * mm});
            skLineSegment(sketch, "E458", {"start": v(8.55, -0.61) * mm, "end": v(9.02, -1.25) * mm});
            skLineSegment(sketch, "E459", {"start": v(9.02, -1.25) * mm, "end": v(9.45, -1.94) * mm});
            skLineSegment(sketch, "E460", {"start": v(9.45, -1.94) * mm, "end": v(9.83, -2.68) * mm});
            skLineSegment(sketch, "E461", {"start": v(9.83, -2.68) * mm, "end": v(10.19, -3.46) * mm});
            skLineSegment(sketch, "E462", {"start": v(10.19, -3.46) * mm, "end": v(10.51, -4.28) * mm});
            skLineSegment(sketch, "E463", {"start": v(10.51, -4.28) * mm, "end": v(10.82, -5.13) * mm});
            skLineSegment(sketch, "E464", {"start": v(10.82, -5.13) * mm, "end": v(11.13, -6) * mm});
            skLineSegment(sketch, "E465", {"start": v(11.13, -6) * mm, "end": v(11.44, -6.9) * mm});
            skLineSegment(sketch, "E466", {"start": v(11.44, -6.9) * mm, "end": v(11.5, -7.06) * mm});
            skLineSegment(sketch, "E467", {"start": v(11.5, -7.06) * mm, "end": v(11.55, -7.21) * mm});
            skLineSegment(sketch, "E468", {"start": v(11.55, -7.21) * mm, "end": v(11.6, -7.37) * mm});
            skLineSegment(sketch, "E469", {"start": v(11.6, -7.37) * mm, "end": v(11.66, -7.52) * mm});
            skLineSegment(sketch, "E470", {"start": v(11.66, -7.52) * mm, "end": v(11.72, -7.67) * mm});
            skLineSegment(sketch, "E471", {"start": v(11.72, -7.67) * mm, "end": v(11.77, -7.83) * mm});
            skLineSegment(sketch, "E472", {"start": v(11.77, -7.83) * mm, "end": v(11.83, -7.98) * mm});
            skLineSegment(sketch, "E473", {"start": v(11.83, -7.98) * mm, "end": v(11.89, -8.13) * mm});
            skLineSegment(sketch, "E474", {"start": v(11.89, -8.13) * mm, "end": v(11.94, -8.29) * mm});
            skLineSegment(sketch, "E475", {"start": v(11.94, -8.29) * mm, "end": v(12, -8.44) * mm});
            skLineSegment(sketch, "E476", {"start": v(12, -8.44) * mm, "end": v(12.05, -8.6) * mm});
            skLineSegment(sketch, "E477", {"start": v(12.05, -8.6) * mm, "end": v(12.11, -8.75) * mm});
            skLineSegment(sketch, "E478", {"start": v(12.11, -8.75) * mm, "end": v(12.17, -8.9) * mm});
            skLineSegment(sketch, "E479", {"start": v(12.17, -8.9) * mm, "end": v(12.22, -9.05) * mm});
            skLineSegment(sketch, "E480", {"start": v(12.22, -9.05) * mm, "end": v(12.28, -9.2) * mm});
            skLineSegment(sketch, "E481", {"start": v(12.28, -9.2) * mm, "end": v(12.34, -9.36) * mm});
            skLineSegment(sketch, "E482", {"start": v(12.34, -9.36) * mm, "end": v(13, -10.72) * mm});
            skLineSegment(sketch, "E483", {"start": v(13, -10.72) * mm, "end": v(13.74, -12.03) * mm});
            skLineSegment(sketch, "E484", {"start": v(13.74, -12.03) * mm, "end": v(14.58, -13.28) * mm});
            skLineSegment(sketch, "E485", {"start": v(14.58, -13.28) * mm, "end": v(15.5, -14.46) * mm});
            skLineSegment(sketch, "E486", {"start": v(15.5, -14.46) * mm, "end": v(16.5, -15.57) * mm});
            skLineSegment(sketch, "E487", {"start": v(16.5, -15.57) * mm, "end": v(17.59, -16.6) * mm});
            skLineSegment(sketch, "E488", {"start": v(17.59, -16.6) * mm, "end": v(18.74, -17.57) * mm});
            skLineSegment(sketch, "E489", {"start": v(18.74, -17.57) * mm, "end": v(19.96, -18.44) * mm});
            skLineSegment(sketch, "E490", {"start": v(19.96, -18.44) * mm, "end": v(21.24, -19.23) * mm});
            skLineSegment(sketch, "E491", {"start": v(21.24, -19.23) * mm, "end": v(22.57, -19.93) * mm});
            skLineSegment(sketch, "E492", {"start": v(22.57, -19.93) * mm, "end": v(23.97, -20.54) * mm});
            skLineSegment(sketch, "E493", {"start": v(23.97, -20.54) * mm, "end": v(25.4, -21.04) * mm});
            skLineSegment(sketch, "E494", {"start": v(25.4, -21.04) * mm, "end": v(26.9, -21.44) * mm});
            skLineSegment(sketch, "E495", {"start": v(26.9, -21.44) * mm, "end": v(28.42, -21.73) * mm});
            skLineSegment(sketch, "E496", {"start": v(28.42, -21.73) * mm, "end": v(29.99, -21.9) * mm});
            skLineSegment(sketch, "E497", {"start": v(29.99, -21.9) * mm, "end": v(31.59, -21.97) * mm});
            skLineSegment(sketch, "E498", {"start": v(31.59, -21.97) * mm, "end": v(33.06, -21.92) * mm});
            skLineSegment(sketch, "E499", {"start": v(33.06, -21.92) * mm, "end": v(34.5, -21.77) * mm});
            skLineSegment(sketch, "E500", {"start": v(34.5, -21.77) * mm, "end": v(35.91, -21.52) * mm});
            skLineSegment(sketch, "E501", {"start": v(35.91, -21.52) * mm, "end": v(37.3, -21.18) * mm});
            skLineSegment(sketch, "E502", {"start": v(37.3, -21.18) * mm, "end": v(38.63, -20.75) * mm});
            skLineSegment(sketch, "E503", {"start": v(38.63, -20.75) * mm, "end": v(39.93, -20.24) * mm});
            skLineSegment(sketch, "E504", {"start": v(39.93, -20.24) * mm, "end": v(41.2, -19.64) * mm});
            skLineSegment(sketch, "E505", {"start": v(41.2, -19.64) * mm, "end": v(42.4, -18.97) * mm});
            skLineSegment(sketch, "E506", {"start": v(42.4, -18.97) * mm, "end": v(43.56, -18.21) * mm});
            skLineSegment(sketch, "E507", {"start": v(43.56, -18.21) * mm, "end": v(44.67, -17.4) * mm});
            skLineSegment(sketch, "E508", {"start": v(44.67, -17.4) * mm, "end": v(45.71, -16.5) * mm});
            skLineSegment(sketch, "E509", {"start": v(45.71, -16.5) * mm, "end": v(46.7, -15.54) * mm});
            skLineSegment(sketch, "E510", {"start": v(46.7, -15.54) * mm, "end": v(47.62, -14.52) * mm});
            skLineSegment(sketch, "E511", {"start": v(47.62, -14.52) * mm, "end": v(48.48, -13.44) * mm});
            skLineSegment(sketch, "E512", {"start": v(48.48, -13.44) * mm, "end": v(49.27, -12.3) * mm});
            skLineSegment(sketch, "E513", {"start": v(49.27, -12.3) * mm, "end": v(49.98, -11.11) * mm});
            skLineSegment(sketch, "E514", {"start": v(49.98, -11.11) * mm, "end": v(50.63, -9.9) * mm});
            skLineSegment(sketch, "E515", {"start": v(50.63, -9.9) * mm, "end": v(51.2, -8.73) * mm});
            skLineSegment(sketch, "E516", {"start": v(51.2, -8.73) * mm, "end": v(51.68, -7.61) * mm});
            skLineSegment(sketch, "E517", {"start": v(51.68, -7.61) * mm, "end": v(52.12, -6.56) * mm});
            skLineSegment(sketch, "E518", {"start": v(52.12, -6.56) * mm, "end": v(52.55, -5.56) * mm});
            skLineSegment(sketch, "E519", {"start": v(52.55, -5.56) * mm, "end": v(53, -4.64) * mm});
            skLineSegment(sketch, "E520", {"start": v(53, -4.64) * mm, "end": v(53.48, -3.78) * mm});
            skLineSegment(sketch, "E521", {"start": v(53.48, -3.78) * mm, "end": v(54.04, -3) * mm});
            skLineSegment(sketch, "E522", {"start": v(54.04, -3) * mm, "end": v(54.7, -2.28) * mm});
            skLineSegment(sketch, "E523", {"start": v(54.7, -2.28) * mm, "end": v(55.5, -1.66) * mm});
            skLineSegment(sketch, "E524", {"start": v(55.5, -1.66) * mm, "end": v(56.45, -1.12) * mm});
            skLineSegment(sketch, "E525", {"start": v(56.45, -1.12) * mm, "end": v(57.6, -0.67) * mm});
            skLineSegment(sketch, "E526", {"start": v(57.6, -0.67) * mm, "end": v(58.95, -0.3) * mm});
            skLineSegment(sketch, "E527", {"start": v(58.95, -0.3) * mm, "end": v(60.55, -0.05) * mm});
            skLineSegment(sketch, "E528", {"start": v(60.55, -0.05) * mm, "end": v(62.43, 0.11) * mm});
            skLineSegment(sketch, "E529", {"start": v(62.43, 0.11) * mm, "end": v(64.62, 0.17) * mm});
            skLineSegment(sketch, "E530", {"start": v(64.62, 0.17) * mm, "end": v(64.62, 0.54) * mm});
            skLineSegment(sketch, "E531", {"start": v(64.62, 0.54) * mm, "end": v(64.62, 0.85) * mm});
            skLineSegment(sketch, "E532", {"start": v(64.62, 0.85) * mm, "end": v(64.62, 1.1) * mm});
            skLineSegment(sketch, "E533", {"start": v(64.62, 1.1) * mm, "end": v(64.62, 1.31) * mm});
            skLineSegment(sketch, "E534", {"start": v(64.62, 1.31) * mm, "end": v(64.62, 1.48) * mm});
            skLineSegment(sketch, "E535", {"start": v(64.62, 1.48) * mm, "end": v(64.62, 1.63) * mm});
            skLineSegment(sketch, "E536", {"start": v(64.62, 1.63) * mm, "end": v(64.62, 1.76) * mm});
            skLineSegment(sketch, "E537", {"start": v(64.62, 1.76) * mm, "end": v(64.62, 1.87) * mm});
            skLineSegment(sketch, "E538", {"start": v(64.62, 1.87) * mm, "end": v(64.62, 1.99) * mm});
            skLineSegment(sketch, "E539", {"start": v(64.62, 1.99) * mm, "end": v(64.62, 2.1) * mm});
            skLineSegment(sketch, "E540", {"start": v(64.62, 2.1) * mm, "end": v(64.62, 2.25) * mm});
            skLineSegment(sketch, "E541", {"start": v(64.62, 2.25) * mm, "end": v(64.62, 2.42) * mm});
            skLineSegment(sketch, "E542", {"start": v(64.62, 2.42) * mm, "end": v(64.62, 2.62) * mm});
            skLineSegment(sketch, "E543", {"start": v(64.62, 2.62) * mm, "end": v(64.62, 2.86) * mm});
            skLineSegment(sketch, "E544", {"start": v(64.62, 2.86) * mm, "end": v(64.62, 3.16) * mm});
            skLineSegment(sketch, "E545", {"start": v(64.62, 3.16) * mm, "end": v(64.62, 3.52) * mm});
            skLineSegment(sketch, "E546", {"start": v(64.62, 3.52) * mm, "end": v(63.55, 3.53) * mm});
            skLineSegment(sketch, "E547", {"start": v(-12.52, -2.74) * mm, "end": v(-12.78, -4.47) * mm});
            skLineSegment(sketch, "E548", {"start": v(-12.78, -4.47) * mm, "end": v(-13.21, -6.15) * mm});
            skLineSegment(sketch, "E549", {"start": v(-13.21, -6.15) * mm, "end": v(-13.8, -7.75) * mm});
            skLineSegment(sketch, "E550", {"start": v(-13.8, -7.75) * mm, "end": v(-14.54, -9.28) * mm});
            skLineSegment(sketch, "E551", {"start": v(-14.54, -9.28) * mm, "end": v(-15.42, -10.72) * mm});
            skLineSegment(sketch, "E552", {"start": v(-15.42, -10.72) * mm, "end": v(-16.42, -12.07) * mm});
            skLineSegment(sketch, "E553", {"start": v(-16.42, -12.07) * mm, "end": v(-17.55, -13.31) * mm});
            skLineSegment(sketch, "E554", {"start": v(-17.55, -13.31) * mm, "end": v(-18.8, -14.44) * mm});
            skLineSegment(sketch, "E555", {"start": v(-18.8, -14.44) * mm, "end": v(-20.14, -15.45) * mm});
            skLineSegment(sketch, "E556", {"start": v(-20.14, -15.45) * mm, "end": v(-21.58, -16.32) * mm});
            skLineSegment(sketch, "E557", {"start": v(-21.58, -16.32) * mm, "end": v(-23.11, -17.06) * mm});
            skLineSegment(sketch, "E558", {"start": v(-23.11, -17.06) * mm, "end": v(-24.72, -17.65) * mm});
            skLineSegment(sketch, "E559", {"start": v(-24.72, -17.65) * mm, "end": v(-26.4, -18.08) * mm});
            skLineSegment(sketch, "E560", {"start": v(-26.4, -18.08) * mm, "end": v(-28.13, -18.35) * mm});
            skLineSegment(sketch, "E561", {"start": v(-28.13, -18.35) * mm, "end": v(-29.91, -18.44) * mm});
            skLineSegment(sketch, "E562", {"start": v(-29.91, -18.44) * mm, "end": v(-31.7, -18.35) * mm});
            skLineSegment(sketch, "E563", {"start": v(-31.7, -18.35) * mm, "end": v(-33.43, -18.08) * mm});
            skLineSegment(sketch, "E564", {"start": v(-33.43, -18.08) * mm, "end": v(-35.1, -17.65) * mm});
            skLineSegment(sketch, "E565", {"start": v(-35.1, -17.65) * mm, "end": v(-36.71, -17.06) * mm});
            skLineSegment(sketch, "E566", {"start": v(-36.71, -17.06) * mm, "end": v(-38.24, -16.32) * mm});
            skLineSegment(sketch, "E567", {"start": v(-38.24, -16.32) * mm, "end": v(-39.68, -15.45) * mm});
            skLineSegment(sketch, "E568", {"start": v(-39.68, -15.45) * mm, "end": v(-41.03, -14.44) * mm});
            skLineSegment(sketch, "E569", {"start": v(-41.03, -14.44) * mm, "end": v(-42.27, -13.31) * mm});
            skLineSegment(sketch, "E570", {"start": v(-42.27, -13.31) * mm, "end": v(-43.4, -12.07) * mm});
            skLineSegment(sketch, "E571", {"start": v(-43.4, -12.07) * mm, "end": v(-44.4, -10.72) * mm});
            skLineSegment(sketch, "E572", {"start": v(-44.4, -10.72) * mm, "end": v(-45.28, -9.28) * mm});
            skLineSegment(sketch, "E573", {"start": v(-45.28, -9.28) * mm, "end": v(-46.02, -7.75) * mm});
            skLineSegment(sketch, "E574", {"start": v(-46.02, -7.75) * mm, "end": v(-46.61, -6.15) * mm});
            skLineSegment(sketch, "E575", {"start": v(-46.61, -6.15) * mm, "end": v(-47.04, -4.47) * mm});
            skLineSegment(sketch, "E576", {"start": v(-47.04, -4.47) * mm, "end": v(-47.3, -2.74) * mm});
            skLineSegment(sketch, "E577", {"start": v(-47.3, -2.74) * mm, "end": v(-47.4, -0.95) * mm});
            skLineSegment(sketch, "E578", {"start": v(-47.4, -0.95) * mm, "end": v(-47.3, 0.83) * mm});
            skLineSegment(sketch, "E579", {"start": v(-47.3, 0.83) * mm, "end": v(-47.04, 2.57) * mm});
            skLineSegment(sketch, "E580", {"start": v(-47.04, 2.57) * mm, "end": v(-46.61, 4.24) * mm});
            skLineSegment(sketch, "E581", {"start": v(-46.61, 4.24) * mm, "end": v(-46.02, 5.85) * mm});
            skLineSegment(sketch, "E582", {"start": v(-46.02, 5.85) * mm, "end": v(-45.28, 7.38) * mm});
            skLineSegment(sketch, "E583", {"start": v(-45.28, 7.38) * mm, "end": v(-44.4, 8.82) * mm});
            skLineSegment(sketch, "E584", {"start": v(-44.4, 8.82) * mm, "end": v(-43.4, 10.16) * mm});
            skLineSegment(sketch, "E585", {"start": v(-43.4, 10.16) * mm, "end": v(-42.27, 11.4) * mm});
            skLineSegment(sketch, "E586", {"start": v(-42.27, 11.4) * mm, "end": v(-41.03, 12.54) * mm});
            skLineSegment(sketch, "E587", {"start": v(-41.03, 12.54) * mm, "end": v(-39.68, 13.54) * mm});
            skLineSegment(sketch, "E588", {"start": v(-39.68, 13.54) * mm, "end": v(-38.24, 14.42) * mm});
            skLineSegment(sketch, "E589", {"start": v(-38.24, 14.42) * mm, "end": v(-36.71, 15.16) * mm});
            skLineSegment(sketch, "E590", {"start": v(-36.71, 15.16) * mm, "end": v(-35.1, 15.75) * mm});
            skLineSegment(sketch, "E591", {"start": v(-35.1, 15.75) * mm, "end": v(-33.43, 16.18) * mm});
            skLineSegment(sketch, "E592", {"start": v(-33.43, 16.18) * mm, "end": v(-31.7, 16.44) * mm});
            skLineSegment(sketch, "E593", {"start": v(-31.7, 16.44) * mm, "end": v(-29.91, 16.53) * mm});
            skLineSegment(sketch, "E594", {"start": v(-29.91, 16.53) * mm, "end": v(-28.13, 16.44) * mm});
            skLineSegment(sketch, "E595", {"start": v(-28.13, 16.44) * mm, "end": v(-26.4, 16.18) * mm});
            skLineSegment(sketch, "E596", {"start": v(-26.4, 16.18) * mm, "end": v(-24.72, 15.75) * mm});
            skLineSegment(sketch, "E597", {"start": v(-24.72, 15.75) * mm, "end": v(-23.11, 15.16) * mm});
            skLineSegment(sketch, "E598", {"start": v(-23.11, 15.16) * mm, "end": v(-21.58, 14.42) * mm});
            skLineSegment(sketch, "E599", {"start": v(-21.58, 14.42) * mm, "end": v(-20.14, 13.54) * mm});
            skLineSegment(sketch, "E600", {"start": v(-20.14, 13.54) * mm, "end": v(-18.8, 12.54) * mm});
            skLineSegment(sketch, "E601", {"start": v(-18.8, 12.54) * mm, "end": v(-17.55, 11.4) * mm});
            skLineSegment(sketch, "E602", {"start": v(-17.55, 11.4) * mm, "end": v(-16.42, 10.16) * mm});
            skLineSegment(sketch, "E603", {"start": v(-16.42, 10.16) * mm, "end": v(-15.42, 8.82) * mm});
            skLineSegment(sketch, "E604", {"start": v(-15.42, 8.82) * mm, "end": v(-14.54, 7.38) * mm});
            skLineSegment(sketch, "E605", {"start": v(-14.54, 7.38) * mm, "end": v(-13.8, 5.85) * mm});
            skLineSegment(sketch, "E606", {"start": v(-13.8, 5.85) * mm, "end": v(-13.21, 4.24) * mm});
            skLineSegment(sketch, "E607", {"start": v(-13.21, 4.24) * mm, "end": v(-12.78, 2.57) * mm});
            skLineSegment(sketch, "E608", {"start": v(-12.78, 2.57) * mm, "end": v(-12.52, 0.83) * mm});
            skLineSegment(sketch, "E609", {"start": v(-12.52, 0.83) * mm, "end": v(-12.43, -0.95) * mm});
            skLineSegment(sketch, "E610", {"start": v(-12.43, -0.95) * mm, "end": v(-12.52, -2.74) * mm});
            skLineSegment(sketch, "E611", {"start": v(48.98, -2.74) * mm, "end": v(48.72, -4.47) * mm});
            skLineSegment(sketch, "E612", {"start": v(48.72, -4.47) * mm, "end": v(48.29, -6.15) * mm});
            skLineSegment(sketch, "E613", {"start": v(48.29, -6.15) * mm, "end": v(47.7, -7.75) * mm});
            skLineSegment(sketch, "E614", {"start": v(47.7, -7.75) * mm, "end": v(46.96, -9.28) * mm});
            skLineSegment(sketch, "E615", {"start": v(46.96, -9.28) * mm, "end": v(46.08, -10.72) * mm});
            skLineSegment(sketch, "E616", {"start": v(46.08, -10.72) * mm, "end": v(45.08, -12.07) * mm});
            skLineSegment(sketch, "E617", {"start": v(45.08, -12.07) * mm, "end": v(43.95, -13.31) * mm});
            skLineSegment(sketch, "E618", {"start": v(43.95, -13.31) * mm, "end": v(42.7, -14.44) * mm});
            skLineSegment(sketch, "E619", {"start": v(42.7, -14.44) * mm, "end": v(41.36, -15.45) * mm});
            skLineSegment(sketch, "E620", {"start": v(41.36, -15.45) * mm, "end": v(39.92, -16.32) * mm});
            skLineSegment(sketch, "E621", {"start": v(39.92, -16.32) * mm, "end": v(38.39, -17.06) * mm});
            skLineSegment(sketch, "E622", {"start": v(38.39, -17.06) * mm, "end": v(36.78, -17.65) * mm});
            skLineSegment(sketch, "E623", {"start": v(36.78, -17.65) * mm, "end": v(35.1, -18.08) * mm});
            skLineSegment(sketch, "E624", {"start": v(35.1, -18.08) * mm, "end": v(33.37, -18.35) * mm});
            skLineSegment(sketch, "E625", {"start": v(33.37, -18.35) * mm, "end": v(31.59, -18.44) * mm});
            skLineSegment(sketch, "E626", {"start": v(31.59, -18.44) * mm, "end": v(29.8, -18.35) * mm});
            skLineSegment(sketch, "E627", {"start": v(29.8, -18.35) * mm, "end": v(28.07, -18.08) * mm});
            skLineSegment(sketch, "E628", {"start": v(28.07, -18.08) * mm, "end": v(26.4, -17.65) * mm});
            skLineSegment(sketch, "E629", {"start": v(26.4, -17.65) * mm, "end": v(24.79, -17.06) * mm});
            skLineSegment(sketch, "E630", {"start": v(24.79, -17.06) * mm, "end": v(23.26, -16.32) * mm});
            skLineSegment(sketch, "E631", {"start": v(23.26, -16.32) * mm, "end": v(21.82, -15.45) * mm});
            skLineSegment(sketch, "E632", {"start": v(21.82, -15.45) * mm, "end": v(20.47, -14.44) * mm});
            skLineSegment(sketch, "E633", {"start": v(20.47, -14.44) * mm, "end": v(19.23, -13.31) * mm});
            skLineSegment(sketch, "E634", {"start": v(19.23, -13.31) * mm, "end": v(18.1, -12.07) * mm});
            skLineSegment(sketch, "E635", {"start": v(18.1, -12.07) * mm, "end": v(17.1, -10.72) * mm});
            skLineSegment(sketch, "E636", {"start": v(17.1, -10.72) * mm, "end": v(16.22, -9.28) * mm});
            skLineSegment(sketch, "E637", {"start": v(16.22, -9.28) * mm, "end": v(15.48, -7.75) * mm});
            skLineSegment(sketch, "E638", {"start": v(15.48, -7.75) * mm, "end": v(14.89, -6.15) * mm});
            skLineSegment(sketch, "E639", {"start": v(14.89, -6.15) * mm, "end": v(14.46, -4.47) * mm});
            skLineSegment(sketch, "E640", {"start": v(14.46, -4.47) * mm, "end": v(14.2, -2.74) * mm});
            skLineSegment(sketch, "E641", {"start": v(14.2, -2.74) * mm, "end": v(14.1, -0.95) * mm});
            skLineSegment(sketch, "E642", {"start": v(14.1, -0.95) * mm, "end": v(14.2, 0.83) * mm});
            skLineSegment(sketch, "E643", {"start": v(14.2, 0.83) * mm, "end": v(14.46, 2.57) * mm});
            skLineSegment(sketch, "E644", {"start": v(14.46, 2.57) * mm, "end": v(14.89, 4.24) * mm});
            skLineSegment(sketch, "E645", {"start": v(14.89, 4.24) * mm, "end": v(15.48, 5.85) * mm});
            skLineSegment(sketch, "E646", {"start": v(15.48, 5.85) * mm, "end": v(16.22, 7.38) * mm});
            skLineSegment(sketch, "E647", {"start": v(16.22, 7.38) * mm, "end": v(17.1, 8.82) * mm});
            skLineSegment(sketch, "E648", {"start": v(17.1, 8.82) * mm, "end": v(18.1, 10.16) * mm});
            skLineSegment(sketch, "E649", {"start": v(18.1, 10.16) * mm, "end": v(19.23, 11.4) * mm});
            skLineSegment(sketch, "E650", {"start": v(19.23, 11.4) * mm, "end": v(20.47, 12.54) * mm});
            skLineSegment(sketch, "E651", {"start": v(20.47, 12.54) * mm, "end": v(21.82, 13.54) * mm});
            skLineSegment(sketch, "E652", {"start": v(21.82, 13.54) * mm, "end": v(23.26, 14.42) * mm});
            skLineSegment(sketch, "E653", {"start": v(23.26, 14.42) * mm, "end": v(24.79, 15.16) * mm});
            skLineSegment(sketch, "E654", {"start": v(24.79, 15.16) * mm, "end": v(26.4, 15.75) * mm});
            skLineSegment(sketch, "E655", {"start": v(26.4, 15.75) * mm, "end": v(28.07, 16.18) * mm});
            skLineSegment(sketch, "E656", {"start": v(28.07, 16.18) * mm, "end": v(29.8, 16.44) * mm});
            skLineSegment(sketch, "E657", {"start": v(29.8, 16.44) * mm, "end": v(31.59, 16.53) * mm});
            skLineSegment(sketch, "E658", {"start": v(31.59, 16.53) * mm, "end": v(33.37, 16.44) * mm});
            skLineSegment(sketch, "E659", {"start": v(33.37, 16.44) * mm, "end": v(35.1, 16.18) * mm});
            skLineSegment(sketch, "E660", {"start": v(35.1, 16.18) * mm, "end": v(36.78, 15.75) * mm});
            skLineSegment(sketch, "E661", {"start": v(36.78, 15.75) * mm, "end": v(38.39, 15.16) * mm});
            skLineSegment(sketch, "E662", {"start": v(38.39, 15.16) * mm, "end": v(39.92, 14.42) * mm});
            skLineSegment(sketch, "E663", {"start": v(39.92, 14.42) * mm, "end": v(41.36, 13.54) * mm});
            skLineSegment(sketch, "E664", {"start": v(41.36, 13.54) * mm, "end": v(42.7, 12.54) * mm});
            skLineSegment(sketch, "E665", {"start": v(42.7, 12.54) * mm, "end": v(43.95, 11.4) * mm});
            skLineSegment(sketch, "E666", {"start": v(43.95, 11.4) * mm, "end": v(45.08, 10.16) * mm});
            skLineSegment(sketch, "E667", {"start": v(45.08, 10.16) * mm, "end": v(46.08, 8.82) * mm});
            skLineSegment(sketch, "E668", {"start": v(46.08, 8.82) * mm, "end": v(46.96, 7.38) * mm});
            skLineSegment(sketch, "E669", {"start": v(46.96, 7.38) * mm, "end": v(47.7, 5.85) * mm});
            skLineSegment(sketch, "E670", {"start": v(47.7, 5.85) * mm, "end": v(48.29, 4.24) * mm});
            skLineSegment(sketch, "E671", {"start": v(48.29, 4.24) * mm, "end": v(48.72, 2.57) * mm});
            skLineSegment(sketch, "E672", {"start": v(48.72, 2.57) * mm, "end": v(48.98, 0.83) * mm});
            skLineSegment(sketch, "E673", {"start": v(48.98, 0.83) * mm, "end": v(49.07, -0.95) * mm});
            skLineSegment(sketch, "E674", {"start": v(49.07, -0.95) * mm, "end": v(48.98, -2.74) * mm});
            skSolve(sketch);
        }
        {
            var Q0;
            Q0 = qSketchRegion(id + "F0", true);
            extrude(context, id + "F1", {"entities" : qUnion([Q0]), "depth" : 6 * mm});
        }
    });
